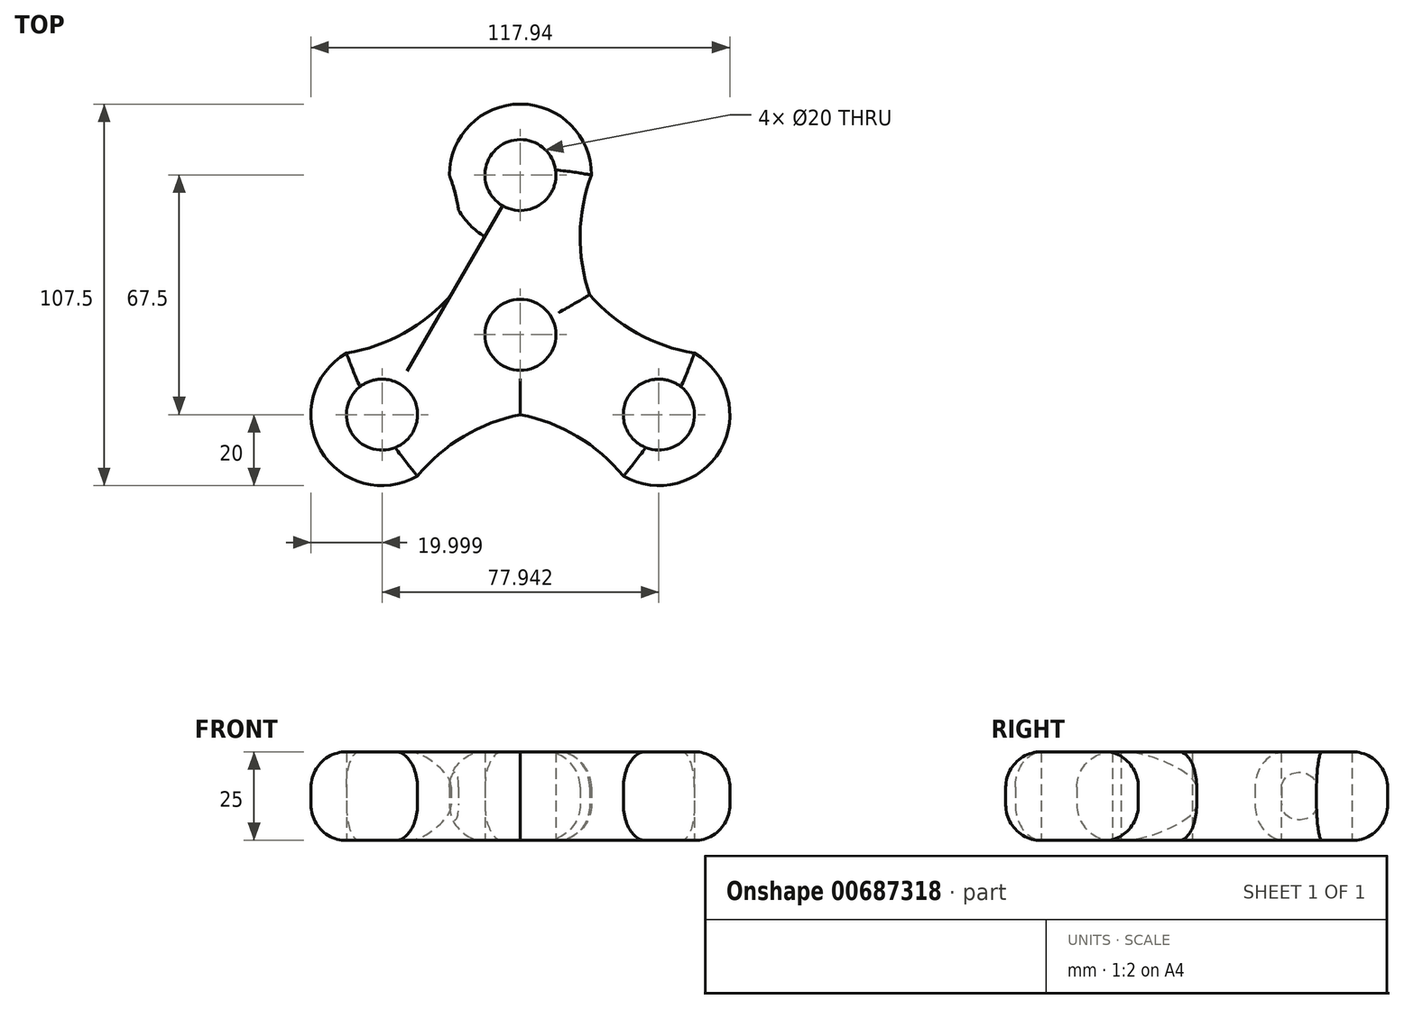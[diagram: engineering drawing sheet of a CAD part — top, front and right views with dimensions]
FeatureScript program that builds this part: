
annotation { "Feature Type Name" : "Feature", "Feature Type Description" : "" }
export const myFeature = defineFeature(function(context is Context, id is Id, definition is map)
    precondition{}
    {
        {
            var Q0;
            Q0=qCreatedBy(makeId("Top.planeOp"),FACE);
            var sketch = newSketch(context, id + "F0", { "sketchPlane" : qUnion([Q0])});
            skLineSegment(sketch, "E0", {"start": v(0, 25) * mm, "end": v(-38.97, -42.5) * mm});
            skLineSegment(sketch, "E1", {"start": v(-38.97, -42.5) * mm, "end": v(38.97, -42.5) * mm});
            skLineSegment(sketch, "E2", {"start": v(38.97, -42.5) * mm, "end": v(0, 25) * mm});
            skLineSegment(sketch, "E3", {"start": v(38.97, -42.5) * mm, "end": v(-19.49, -8.75) * mm, "construction": true});
            skLineSegment(sketch, "E4", {"start": v(-38.97, -42.5) * mm, "end": v(19.49, -8.75) * mm, "construction": true});
            skLineSegment(sketch, "E5", {"start": v(0, 25) * mm, "end": v(0, -42.5) * mm, "construction": true});
            skCircle(sketch, "E6", {"center": v(0, -20) * mm, "radius": 10 * mm});
            skCircle(sketch, "E7", {"center": v(-38.97, -42.5) * mm, "radius": 20 * mm});
            skCircle(sketch, "E8", {"center": v(-38.97, -42.5) * mm, "radius": 10 * mm});
            skCircle(sketch, "E9.1.0", {"center": v(38.97, -42.5) * mm, "radius": 20 * mm});
            skCircle(sketch, "E9.1.1", {"center": v(38.97, -42.5) * mm, "radius": 10 * mm});
            skCircle(sketch, "E9.2.0", {"center": v(0, 25) * mm, "radius": 20 * mm});
            skCircle(sketch, "E9.2.1", {"center": v(0, 25) * mm, "radius": 10 * mm});
            skArc(sketch, "E10", {"start": v(-19.49, -8.75) * mm, "mid": v(-16.8, 8.17) * mm, "end": v(-20, 25) * mm});
            skArc(sketch, "E11.1.0", {"start": v(0, -42.5) * mm, "mid": v(-16, -48.64) * mm, "end": v(-28.97, -59.82) * mm});
            skArc(sketch, "E11.2.0", {"start": v(19.49, -8.75) * mm, "mid": v(32.8, -19.53) * mm, "end": v(48.97, -25.18) * mm});
            skArc(sketch, "E12", {"start": v(20, 25) * mm, "mid": v(16.8, 8.17) * mm, "end": v(19.49, -8.75) * mm});
            skArc(sketch, "E13.1.0", {"start": v(-48.97, -25.18) * mm, "mid": v(-32.8, -19.53) * mm, "end": v(-19.49, -8.75) * mm});
            skArc(sketch, "E13.2.0", {"start": v(28.97, -59.82) * mm, "mid": v(16, -48.64) * mm, "end": v(0, -42.5) * mm});
            skSolve(sketch);
        }
        {
            var Q0;
            {var subQ0=sQuery(id+"F0.wireOp",EDGE,"E13.1.0");var subQ3=sQuery(id+"F0.wireOp",EDGE,"E7");var subQ5=makeQuery(id+"F0.imprint","INTERSECT",VERTEX,{"disambiguationData":[OD(1.0)],"derivedFrom":[subQ3,subQ0]});Q0=makeQuery(id+"F0.imprint","IMPRINT",FACE,{"disambiguationData":[TD([[makeQuery(id+"F0.imprint","IMPRINT",EDGE,{"disambiguationData":[TD([[subQ5,1.0]])],"derivedFrom":subQ3}),-1.0]])]});}
            var Q1;
            {var subQ1=sQuery(id+"F0.wireOp",EDGE,"E7");var subQ3=sQuery(id+"F0.wireOp",EDGE,"E0");var subQ4=makeQuery(id+"F0.imprint","INTERSECT",VERTEX,{"derivedFrom":[subQ3,subQ1]});Q1=makeQuery(id+"F0.imprint","IMPRINT",FACE,{"disambiguationData":[TD([[makeQuery(id+"F0.imprint","IMPRINT",EDGE,{"disambiguationData":[TD([[subQ4,-1.0]])],"derivedFrom":subQ3}),-1.0]])]});}
            var Q2;
            {var subQ0=sQuery(id+"F0.wireOp",EDGE,"E11.1.0");var subQ3=sQuery(id+"F0.wireOp",EDGE,"E7");var subQ5=makeQuery(id+"F0.imprint","INTERSECT",VERTEX,{"disambiguationData":[OD(1.0)],"derivedFrom":[subQ3,subQ0]});Q2=makeQuery(id+"F0.imprint","IMPRINT",FACE,{"disambiguationData":[TD([[makeQuery(id+"F0.imprint","IMPRINT",EDGE,{"disambiguationData":[TD([[subQ5,-1.0]])],"derivedFrom":subQ3}),-1.0]])]});}
            var Q3;
            {var subQ0=sQuery(id+"F0.wireOp",EDGE,"E13.2.0");var subQ3=sQuery(id+"F0.wireOp",EDGE,"E9.1.0");var subQ5=makeQuery(id+"F0.imprint","INTERSECT",VERTEX,{"disambiguationData":[OD(1.0)],"derivedFrom":[subQ3,subQ0]});Q3=makeQuery(id+"F0.imprint","IMPRINT",FACE,{"disambiguationData":[TD([[makeQuery(id+"F0.imprint","IMPRINT",EDGE,{"disambiguationData":[TD([[subQ5,1.0]])],"derivedFrom":subQ3}),-1.0]])]});}
            var Q4;
            {var subQ1=sQuery(id+"F0.wireOp",EDGE,"E9.1.0");var subQ3=sQuery(id+"F0.wireOp",EDGE,"E1");var subQ4=makeQuery(id+"F0.imprint","INTERSECT",VERTEX,{"derivedFrom":[subQ3,subQ1]});Q4=makeQuery(id+"F0.imprint","IMPRINT",FACE,{"disambiguationData":[TD([[makeQuery(id+"F0.imprint","IMPRINT",EDGE,{"disambiguationData":[TD([[subQ4,-1.0]])],"derivedFrom":subQ3}),-1.0]])]});}
            var Q5;
            {var subQ0=sQuery(id+"F0.wireOp",EDGE,"E11.2.0");var subQ3=sQuery(id+"F0.wireOp",EDGE,"E9.1.0");var subQ5=makeQuery(id+"F0.imprint","INTERSECT",VERTEX,{"disambiguationData":[OD(1.0)],"derivedFrom":[subQ3,subQ0]});Q5=makeQuery(id+"F0.imprint","IMPRINT",FACE,{"disambiguationData":[TD([[makeQuery(id+"F0.imprint","IMPRINT",EDGE,{"disambiguationData":[TD([[subQ5,-1.0]])],"derivedFrom":subQ3}),-1.0]])]});}
            var Q6;
            Q6=makeQuery(id+"F0.imprint","IMPRINT",FACE,{"disambiguationData":[TD([[makeQuery(id+"F0.imprint","IMPRINT",EDGE,{"derivedFrom":sQuery(id+"F0.wireOp",EDGE,"E6")}),-1.0]])]});
            var Q7;
            {var subQ0=sQuery(id+"F0.wireOp",EDGE,"E10");var subQ3=sQuery(id+"F0.wireOp",EDGE,"E9.2.0");var subQ5=makeQuery(id+"F0.imprint","INTERSECT",VERTEX,{"disambiguationData":[OD(1.0)],"derivedFrom":[subQ3,subQ0]});Q7=makeQuery(id+"F0.imprint","IMPRINT",FACE,{"disambiguationData":[TD([[makeQuery(id+"F0.imprint","IMPRINT",EDGE,{"disambiguationData":[TD([[subQ5,-1.0]])],"derivedFrom":subQ3}),-1.0]])]});}
            var Q8;
            {var subQ0=sQuery(id+"F0.wireOp",EDGE,"E12");var subQ3=sQuery(id+"F0.wireOp",EDGE,"E9.2.0");var subQ5=makeQuery(id+"F0.imprint","INTERSECT",VERTEX,{"disambiguationData":[OD(1.0)],"derivedFrom":[subQ3,subQ0]});Q8=makeQuery(id+"F0.imprint","IMPRINT",FACE,{"disambiguationData":[TD([[makeQuery(id+"F0.imprint","IMPRINT",EDGE,{"disambiguationData":[TD([[subQ5,1.0]])],"derivedFrom":subQ3}),-1.0]])]});}
            var Q9;
            {var subQ7=sQuery(id+"F0.wireOp",EDGE,"E9.2.1");var subQ10=sQuery(id+"F0.wireOp",EDGE,"E0");var subQ11=makeQuery(id+"F0.imprint","INTERSECT",VERTEX,{"derivedFrom":[subQ10,subQ7]});Q9=makeQuery(id+"F0.imprint","IMPRINT",FACE,{"disambiguationData":[TD([[makeQuery(id+"F0.imprint","IMPRINT",EDGE,{"disambiguationData":[TD([[subQ11,-1.0]])],"derivedFrom":subQ10}),-1.0]])]});}
            var Q10;
            {var subQ0=sQuery(id+"F0.wireOp",EDGE,"E9.2.1");var subQ1=sQuery(id+"F0.wireOp",EDGE,"E0");var subQ2=makeQuery(id+"F0.imprint","INTERSECT",VERTEX,{"derivedFrom":[subQ1,subQ0]});Q10=makeQuery(id+"F0.imprint","IMPRINT",FACE,{"disambiguationData":[TD([[makeQuery(id+"F0.imprint","IMPRINT",EDGE,{"disambiguationData":[TD([[subQ2,-1.0]])],"derivedFrom":subQ1}),1.0]])]});}
            var Q11;
            {var subQ0=sQuery(id+"F0.wireOp",EDGE,"E7");var subQ1=sQuery(id+"F0.wireOp",EDGE,"E0");var subQ2=makeQuery(id+"F0.imprint","INTERSECT",VERTEX,{"derivedFrom":[subQ1,subQ0]});Q11=makeQuery(id+"F0.imprint","IMPRINT",FACE,{"disambiguationData":[TD([[makeQuery(id+"F0.imprint","IMPRINT",EDGE,{"disambiguationData":[TD([[subQ2,-1.0]])],"derivedFrom":subQ1}),1.0]])]});}
            var Q12;
            {var subQ0=sQuery(id+"F0.wireOp",EDGE,"E9.1.0");var subQ1=sQuery(id+"F0.wireOp",EDGE,"E1");var subQ2=makeQuery(id+"F0.imprint","INTERSECT",VERTEX,{"derivedFrom":[subQ1,subQ0]});Q12=makeQuery(id+"F0.imprint","IMPRINT",FACE,{"disambiguationData":[TD([[makeQuery(id+"F0.imprint","IMPRINT",EDGE,{"disambiguationData":[TD([[subQ2,-1.0]])],"derivedFrom":subQ1}),1.0]])]});}
            extrude(context, id + "F1", {"entities" : qUnion([Q0, Q1, Q2, Q3, Q4, Q5, Q6, Q7, Q8, Q9, Q10, Q11, Q12]), "depth" : 25 * mm, "offsetDistance" : 25 * mm});
        }
        {
            var Q0;
            Q0=makeQuery(id+"F1.opExtrude","CAP_EDGE",EDGE,{"disambiguationData":[OSD([sQuery(id+"F0.wireOp",EDGE,"E10")])],"isStart":false});
            var Q1;
            Q1=makeQuery(id+"F1.opExtrude","CAP_EDGE",EDGE,{"disambiguationData":[OSD([sQuery(id+"F0.wireOp",EDGE,"E13.1.0")])],"isStart":false});
            var Q2;
            Q2=makeQuery(id+"F1.opExtrude","CAP_EDGE",EDGE,{"disambiguationData":[OSD([sQuery(id+"F0.wireOp",EDGE,"E7")])],"isStart":false});
            var Q3;
            Q3=makeQuery(id+"F1.opExtrude","CAP_EDGE",EDGE,{"disambiguationData":[OSD([sQuery(id+"F0.wireOp",EDGE,"E11.1.0")])],"isStart":false});
            var Q4;
            Q4=makeQuery(id+"F1.opExtrude","CAP_EDGE",EDGE,{"disambiguationData":[OSD([sQuery(id+"F0.wireOp",EDGE,"E13.2.0")])],"isStart":false});
            var Q5;
            Q5=makeQuery(id+"F1.opExtrude","CAP_EDGE",EDGE,{"disambiguationData":[OSD([sQuery(id+"F0.wireOp",EDGE,"E9.1.0")])],"isStart":false});
            var Q6;
            Q6=makeQuery(id+"F1.opExtrude","CAP_EDGE",EDGE,{"disambiguationData":[OSD([sQuery(id+"F0.wireOp",EDGE,"E11.2.0")])],"isStart":false});
            var Q7;
            Q7=makeQuery(id+"F1.opExtrude","CAP_EDGE",EDGE,{"disambiguationData":[OSD([sQuery(id+"F0.wireOp",EDGE,"E12")])],"isStart":false});
            var Q8;
            Q8=makeQuery(id+"F1.opExtrude","CAP_EDGE",EDGE,{"disambiguationData":[OSD([sQuery(id+"F0.wireOp",EDGE,"E9.2.0")])],"isStart":false});
            var Q9;
            Q9=makeQuery(id+"F1.opExtrude","CAP_EDGE",EDGE,{"disambiguationData":[OSD([sQuery(id+"F0.wireOp",EDGE,"E7")])],"isStart":true});
            var Q10;
            Q10=makeQuery(id+"F1.opExtrude","CAP_EDGE",EDGE,{"disambiguationData":[OSD([sQuery(id+"F0.wireOp",EDGE,"E11.1.0")])],"isStart":true});
            var Q11;
            Q11=makeQuery(id+"F1.opExtrude","CAP_EDGE",EDGE,{"disambiguationData":[OSD([sQuery(id+"F0.wireOp",EDGE,"E13.1.0")])],"isStart":true});
            var Q12;
            Q12=makeQuery(id+"F1.opExtrude","CAP_EDGE",EDGE,{"disambiguationData":[OSD([sQuery(id+"F0.wireOp",EDGE,"E10")])],"isStart":true});
            var Q13;
            Q13=makeQuery(id+"F1.opExtrude","CAP_EDGE",EDGE,{"disambiguationData":[OSD([sQuery(id+"F0.wireOp",EDGE,"E9.2.0")])],"isStart":true});
            var Q14;
            Q14=makeQuery(id+"F1.opExtrude","CAP_EDGE",EDGE,{"disambiguationData":[OSD([sQuery(id+"F0.wireOp",EDGE,"E12")])],"isStart":true});
            var Q15;
            Q15=makeQuery(id+"F1.opExtrude","CAP_EDGE",EDGE,{"disambiguationData":[OSD([sQuery(id+"F0.wireOp",EDGE,"E11.2.0")])],"isStart":true});
            var Q16;
            Q16=makeQuery(id+"F1.opExtrude","CAP_EDGE",EDGE,{"disambiguationData":[OSD([sQuery(id+"F0.wireOp",EDGE,"E13.2.0")])],"isStart":true});
            var Q17;
            Q17=makeQuery(id+"F1.opExtrude","CAP_EDGE",EDGE,{"disambiguationData":[OSD([sQuery(id+"F0.wireOp",EDGE,"E9.1.0")])],"isStart":true});
            fillet(context, id + "F2", {"entities" : qUnion([Q0, Q1, Q2, Q3, Q4, Q5, Q6, Q7, Q8, Q9, Q10, Q11, Q12, Q13, Q14, Q15, Q16, Q17]), "radius" : 10 * mm, "tangentPropagation" : true, "allowEdgeOverflow" : false});
        }
    });
